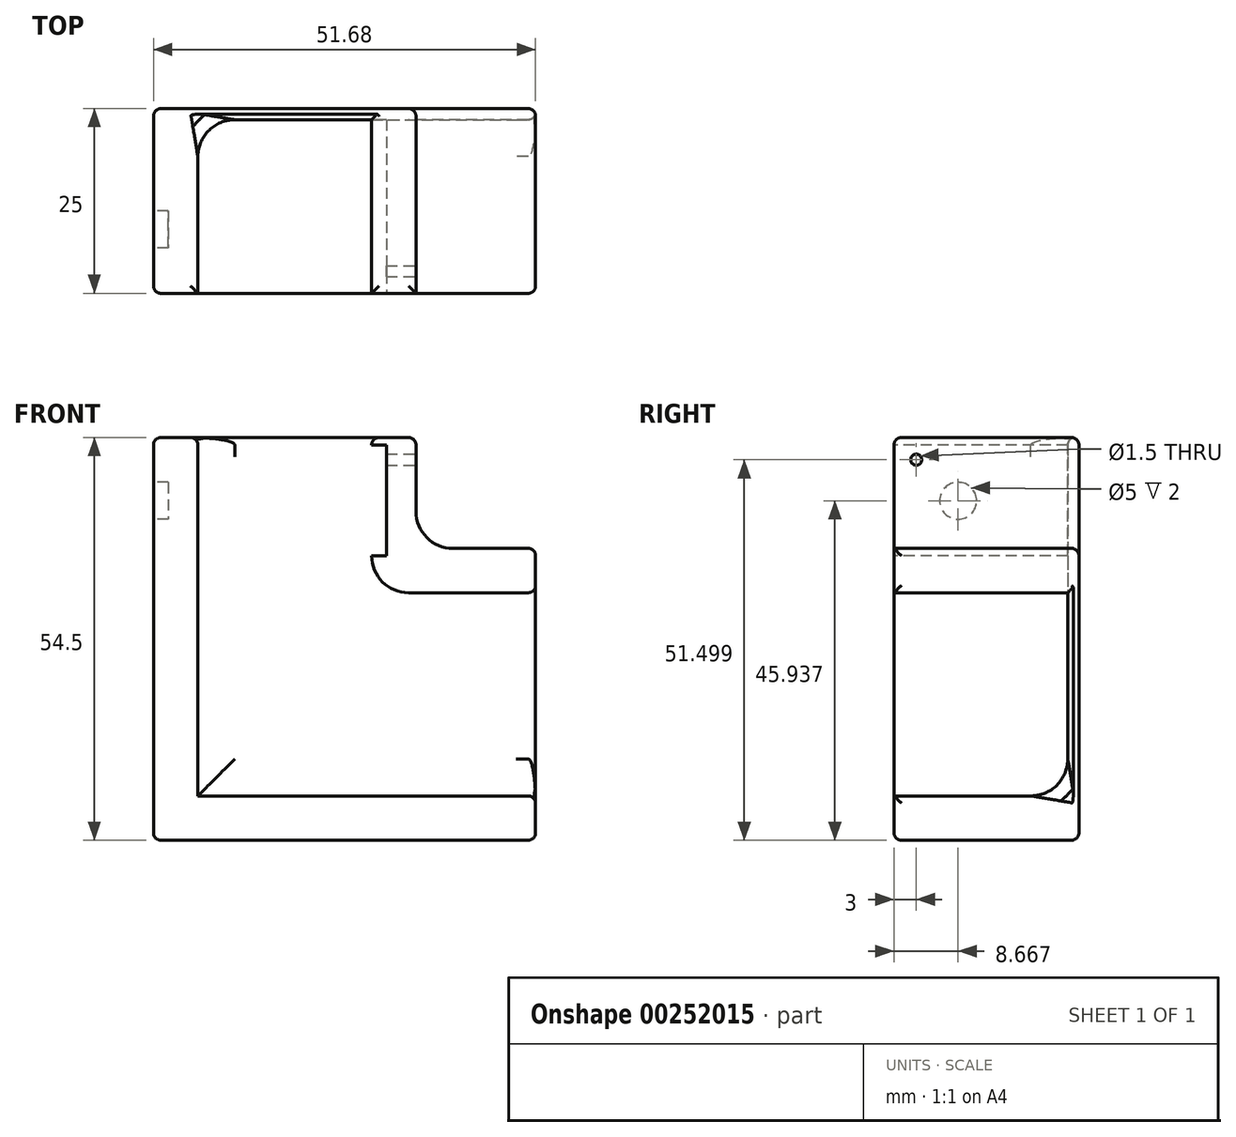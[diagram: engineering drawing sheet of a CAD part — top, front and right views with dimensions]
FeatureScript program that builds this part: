
annotation { "Feature Type Name" : "Feature", "Feature Type Description" : "" }
export const myFeature = defineFeature(function(context is Context, id is Id, definition is map)
    precondition{}
    {
        {
            var Q0;
            Q0=qCreatedBy(makeId("Front.planeOp"),FACE);
            var sketch = newSketch(context, id + "F0", { "sketchPlane" : qUnion([Q0])});
            skLineSegment(sketch, "E0.bottom", {"start": v(2.9, 7.88) * mm, "end": v(19.08, 7.88) * mm});
            skLineSegment(sketch, "E0.left", {"start": v(2.9, 7.88) * mm, "end": v(2.9, 22.88) * mm});
            skLineSegment(sketch, "E1.bottom", {"start": v(2.9, 22.88) * mm, "end": v(-20.6, 22.88) * mm});
            skLineSegment(sketch, "E1.top", {"start": v(19.08, -19.62) * mm, "end": v(-20.6, -19.62) * mm});
            skLineSegment(sketch, "E1.left", {"start": v(19.08, 7.88) * mm, "end": v(19.08, -19.62) * mm});
            skLineSegment(sketch, "E1.right", {"start": v(-20.6, 22.88) * mm, "end": v(-20.6, -19.62) * mm});
            skLineSegment(sketch, "E2.0", {"start": v(8.9, 13.88) * mm, "end": v(25.08, 13.88) * mm});
            skLineSegment(sketch, "E2.1", {"start": v(8.9, 28.88) * mm, "end": v(-26.6, 28.88) * mm});
            skLineSegment(sketch, "E2.2", {"start": v(-26.6, 28.88) * mm, "end": v(-26.6, -25.62) * mm});
            skLineSegment(sketch, "E2.3", {"start": v(8.9, 13.88) * mm, "end": v(8.9, 28.88) * mm});
            skLineSegment(sketch, "E2.4", {"start": v(25.08, -25.62) * mm, "end": v(-26.6, -25.62) * mm});
            skLineSegment(sketch, "E2.5", {"start": v(25.08, 13.88) * mm, "end": v(25.08, -25.62) * mm});
            skSolve(sketch);
        }
        {
            var Q0;
            Q0 = qSketchRegion(id + "F0", true);
            var Q1;
            Q1=makeQuery(id+"F0.imprint","IMPRINT",FACE,{"disambiguationData":[TD([[makeQuery(id+"F0.imprint","IMPRINT",EDGE,{"derivedFrom":sQuery(id+"F0.wireOp",EDGE,"E0.bottom")}),-1.0]])]});
            extrude(context, id + "F1", {"entities" : qUnion([Q0, Q1]), "depth" : 25 * mm});
        }
        {
            var Q0;
            Q0=makeQuery(id+"F1.opExtrude","CAP_FACE",FACE,{"disambiguationData":[OSD([sQuery(id+"F0.wireOp",EDGE,"E2.0"),sQuery(id+"F0.wireOp",EDGE,"E2.1"),sQuery(id+"F0.wireOp",EDGE,"E2.2"),sQuery(id+"F0.wireOp",EDGE,"E2.3"),sQuery(id+"F0.wireOp",EDGE,"E2.4"),sQuery(id+"F0.wireOp",EDGE,"E2.5")])],"isStart":false});
            var sketch = newSketch(context, id + "F2", { "sketchPlane" : qUnion([Q0])});
            skLineSegment(sketch, "E3.0", {"start": v(-20.6, 28.88) * mm, "end": v(-20.6, -19.62) * mm});
            skLineSegment(sketch, "E3.2", {"start": v(25.08, 7.88) * mm, "end": v(2.9, 7.88) * mm});
            skLineSegment(sketch, "E3.3", {"start": v(-20.6, -19.62) * mm, "end": v(25.08, -19.62) * mm});
            skLineSegment(sketch, "E3.4", {"start": v(2.9, 7.88) * mm, "end": v(2.9, 28.88) * mm});
            skSolve(sketch);
        }
        {
            var Q0;
            {var subQ5=sQuery(id+"F2.wireOp",EDGE,"E3.3");var subQ6=sQuery(id+"F2.wireOp",EDGE,"E3.0");var subQ7=makeQuery(id+"F2.imprint","INTERSECT",VERTEX,{"derivedFrom":[subQ6,subQ5]});Q0=makeQuery(id+"F2.imprint","IMPRINT",FACE,{"disambiguationData":[TD([[makeQuery(id+"F2.imprint","IMPRINT",EDGE,{"disambiguationData":[TD([[subQ7,1.0]])],"derivedFrom":subQ6}),1.0]])]});}
            extrude(context, id + "F3", {"entities" : qUnion([Q0]), "operationType" : NewBodyOperationType.REMOVE, "oppositeDirection" : true, "depth" : 23.5 * mm});
        }
        {
            var Q0;
            Q0=makeQuery(id+"F1.opExtrude","SWEPT_EDGE",EDGE,{"disambiguationData":[OSD([sQuery(id+"F0.wireOp",EDGE,"E2.0"),sQuery(id+"F0.wireOp",EDGE,"E2.3")])]});
            var Q1;
            Q1=makeQuery(id+"F3.boolean.opBoolean","COPY",EDGE,{"derivedFrom":makeQuery(id+"F3.opExtrude","SWEPT_EDGE",EDGE,{"disambiguationData":[OSD([sQuery(id+"F2.wireOp",EDGE,"E3.2"),sQuery(id+"F2.wireOp",EDGE,"E3.4")])]})});
            fillet(context, id + "F4", {"entities" : qUnion([Q0, Q1]), "radius" : 5 * mm, "tangentPropagation" : true, "allowEdgeOverflow" : false});
        }
        {
            var Q0;
            Q0=makeQuery(id+"F1.opExtrude","SWEPT_FACE",FACE,{"disambiguationData":[OSD([sQuery(id+"F0.wireOp",EDGE,"E2.5")])]});
            var Q1;
            Q1=makeQuery(id+"F1.opExtrude","SWEPT_FACE",FACE,{"disambiguationData":[OSD([sQuery(id+"F0.wireOp",EDGE,"E2.1")])]});
            var Q2;
            Q2=makeQuery(id+"F1.opExtrude","CAP_FACE",FACE,{"disambiguationData":[OSD([sQuery(id+"F0.wireOp",EDGE,"E2.0"),sQuery(id+"F0.wireOp",EDGE,"E2.1"),sQuery(id+"F0.wireOp",EDGE,"E2.2"),sQuery(id+"F0.wireOp",EDGE,"E2.3"),sQuery(id+"F0.wireOp",EDGE,"E2.4"),sQuery(id+"F0.wireOp",EDGE,"E2.5")])],"isStart":true});
            var Q3;
            Q3=makeQuery(id+"F1.opExtrude","SWEPT_EDGE",EDGE,{"disambiguationData":[OSD([sQuery(id+"F0.wireOp",EDGE,"E2.2"),sQuery(id+"F0.wireOp",EDGE,"E2.4")])]});
            var Q4;
            Q4=makeQuery(id+"F1.opExtrude","CAP_EDGE",EDGE,{"disambiguationData":[OSD([sQuery(id+"F0.wireOp",EDGE,"E2.2")])],"isStart":false});
            var Q5;
            Q5=makeQuery(id+"F1.opExtrude","CAP_EDGE",EDGE,{"disambiguationData":[OSD([sQuery(id+"F0.wireOp",EDGE,"E2.4")])],"isStart":false});
            fillet(context, id + "F5", {"entities" : qUnion([Q0, Q1, Q2, Q3, Q4, Q5]), "radius" : 1 * mm, "tangentPropagation" : true, "allowEdgeOverflow" : false});
        }
        {
            var Q0;
            Q0=makeQuery(id+"F1.opExtrude","SWEPT_FACE",FACE,{"disambiguationData":[OSD([sQuery(id+"F0.wireOp",EDGE,"E2.3")])]});
            var sketch = newSketch(context, id + "F6", { "sketchPlane" : qUnion([Q0])});
            skCircle(sketch, "E4", {"center": v(-22, 25.88) * mm, "radius": 0.75 * mm});
            skSolve(sketch);
        }
        {
            var Q0;
            Q0 = qSketchRegion(id + "F6", true);
            extrude(context, id + "F7", {"entities" : qUnion([Q0]), "operationType" : NewBodyOperationType.REMOVE, "oppositeDirection" : true, "depth" : 25 * mm});
        }
        {
            var Q0;
            Q0=makeQuery(id+"F1.opExtrude","SWEPT_FACE",FACE,{"disambiguationData":[OSD([sQuery(id+"F0.wireOp",EDGE,"E2.2")])]});
            var sketch = newSketch(context, id + "F8", { "sketchPlane" : qUnion([Q0])});
            skCircle(sketch, "E5", {"center": v(16.33, 20.32) * mm, "radius": 2.5 * mm});
            skSolve(sketch);
        }
        {
            var Q0;
            Q0=makeQuery(id+"F3.boolean.opBoolean","COPY",FACE,{"derivedFrom":makeQuery(id+"F3.opExtrude","SWEPT_FACE",FACE,{"disambiguationData":[OSD([sQuery(id+"F2.wireOp",EDGE,"E3.4")])]})});
            var Q1;
            Q1 = qSketchRegion(id + "F8", true);
            extrude(context, id + "F9", {"entities" : qUnion([Q0, Q1]), "operationType" : NewBodyOperationType.REMOVE, "oppositeDirection" : true, "depth" : 2 * mm});
        }
        {
            var Q0;
            Q0=makeQuery(id+"F3.boolean.opBoolean","COPY",EDGE,{"derivedFrom":makeQuery(id+"F3.opExtrude","CAP_EDGE",EDGE,{"disambiguationData":[OSD([sQuery(id+"F2.wireOp",EDGE,"E3.0")])],"isStart":false})});
            var Q1;
            Q1=makeQuery(id+"F3.boolean.opBoolean","COPY",EDGE,{"derivedFrom":makeQuery(id+"F3.opExtrude","CAP_EDGE",EDGE,{"disambiguationData":[OSD([sQuery(id+"F2.wireOp",EDGE,"E3.3")])],"isStart":false})});
            var Q2;
            Q2=makeQuery(id+"F3.boolean.opBoolean","COPY",EDGE,{"derivedFrom":makeQuery(id+"F3.opExtrude","CAP_EDGE",EDGE,{"disambiguationData":[OSD([sQuery(id+"F2.wireOp",EDGE,"E3.4")])],"isStart":false})});
            fillet(context, id + "F10", {"entities" : qUnion([Q0, Q1, Q2]), "radius" : 5 * mm, "tangentPropagation" : true, "allowEdgeOverflow" : false});
        }
    });
